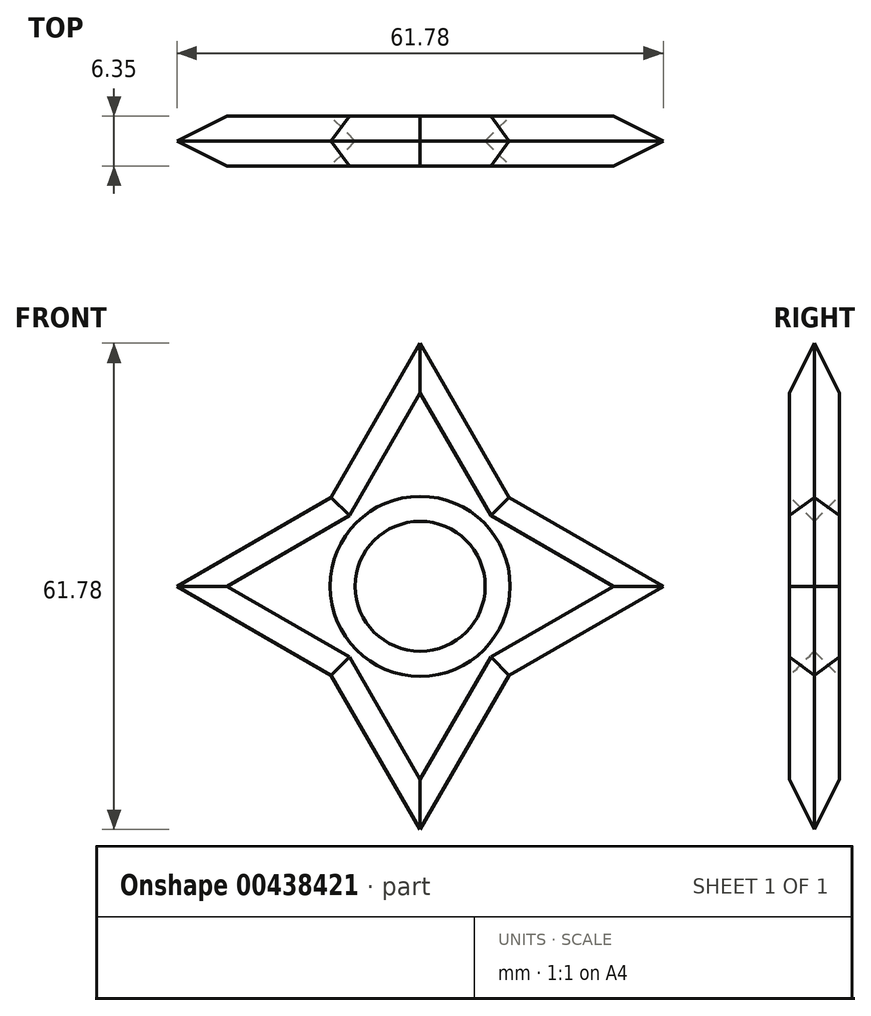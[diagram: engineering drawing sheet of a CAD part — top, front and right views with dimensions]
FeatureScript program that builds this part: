
annotation { "Feature Type Name" : "Feature", "Feature Type Description" : "" }
export const myFeature = defineFeature(function(context is Context, id is Id, definition is map)
    precondition{}
    {
        {
            var Q0;
            Q0=qCreatedBy(makeId("Front.planeOp"),FACE);
            var sketch = newSketch(context, id + "F0", { "sketchPlane" : qUnion([Q0])});
            skLineSegment(sketch, "E0.bottom", {"start": v(0, 0) * mm, "end": v(25.4, 0) * mm});
            skLineSegment(sketch, "E0.top", {"start": v(0, 25.4) * mm, "end": v(25.4, 25.4) * mm});
            skLineSegment(sketch, "E0.left", {"start": v(0, 0) * mm, "end": v(0, 25.4) * mm});
            skLineSegment(sketch, "E0.right", {"start": v(25.4, 0) * mm, "end": v(25.4, 25.4) * mm});
            skLineSegment(sketch, "E1", {"start": v(0, 25.4) * mm, "end": v(12.7, 47.4) * mm});
            skLineSegment(sketch, "E2", {"start": v(12.7, 47.4) * mm, "end": v(25.4, 25.4) * mm});
            skLineSegment(sketch, "E3", {"start": v(0, 25.4) * mm, "end": v(-22, 12.7) * mm});
            skPoint(sketch, "E3.endSnap0", {"position": v(0, 12.7) * mm});
            skLineSegment(sketch, "E4", {"start": v(-22, 12.7) * mm, "end": v(0, 0) * mm});
            skLineSegment(sketch, "E5", {"start": v(0, 0) * mm, "end": v(12.7, -22) * mm});
            skLineSegment(sketch, "E6", {"start": v(12.7, -22) * mm, "end": v(25.4, 0) * mm});
            skLineSegment(sketch, "E7", {"start": v(25.4, 25.4) * mm, "end": v(47.4, 12.7) * mm});
            skLineSegment(sketch, "E8", {"start": v(47.4, 12.7) * mm, "end": v(25.4, 0) * mm});
            skCircle(sketch, "E9", {"center": v(12.7, 12.7) * mm, "radius": 6.35 * mm});
            skSolve(sketch);
        }
        {
            var Q0;
            Q0=makeQuery(id+"F0.imprint","IMPRINT",FACE,{"disambiguationData":[TD([[makeQuery(id+"F0.imprint","IMPRINT",EDGE,{"derivedFrom":sQuery(id+"F0.wireOp",EDGE,"E0.bottom")}),1.0]])]});
            var Q1;
            Q1=makeQuery(id+"F0.imprint","IMPRINT",FACE,{"disambiguationData":[TD([[makeQuery(id+"F0.imprint","IMPRINT",EDGE,{"derivedFrom":sQuery(id+"F0.wireOp",EDGE,"E0.top")}),1.0]])]});
            var Q2;
            Q2=makeQuery(id+"F0.imprint","IMPRINT",FACE,{"disambiguationData":[TD([[makeQuery(id+"F0.imprint","IMPRINT",EDGE,{"derivedFrom":sQuery(id+"F0.wireOp",EDGE,"E0.left")}),1.0]])]});
            var Q3;
            Q3=makeQuery(id+"F0.imprint","IMPRINT",FACE,{"disambiguationData":[TD([[makeQuery(id+"F0.imprint","IMPRINT",EDGE,{"derivedFrom":sQuery(id+"F0.wireOp",EDGE,"E0.right")}),-1.0]])]});
            var Q4;
            Q4=makeQuery(id+"F0.imprint","IMPRINT",FACE,{"disambiguationData":[TD([[makeQuery(id+"F0.imprint","IMPRINT",EDGE,{"derivedFrom":sQuery(id+"F0.wireOp",EDGE,"E0.bottom")}),-1.0]])]});
            extrude(context, id + "F1", {"entities" : qUnion([Q0, Q1, Q2, Q3, Q4]), "depth" : 6.35 * mm});
        }
        {
            var Q0;
            Q0=makeQuery(id+"F1.opExtrude","CAP_FACE",FACE,{"disambiguationData":[OSD([sQuery(id+"F0.wireOp",EDGE,"E1"),sQuery(id+"F0.wireOp",EDGE,"E2"),sQuery(id+"F0.wireOp",EDGE,"E3"),sQuery(id+"F0.wireOp",EDGE,"E4"),sQuery(id+"F0.wireOp",EDGE,"E5"),sQuery(id+"F0.wireOp",EDGE,"E6"),sQuery(id+"F0.wireOp",EDGE,"E7"),sQuery(id+"F0.wireOp",EDGE,"E8")])],"isStart":false});
            chamfer(context, id + "F2", {"entities" : qUnion([Q0]), "width" : 5.08 * mm, "tangentPropagation" : true});
        }
        {
            var Q0;
            Q0=makeQuery(id+"F1.opExtrude","CAP_FACE",FACE,{"disambiguationData":[OSD([sQuery(id+"F0.wireOp",EDGE,"E1"),sQuery(id+"F0.wireOp",EDGE,"E2"),sQuery(id+"F0.wireOp",EDGE,"E3"),sQuery(id+"F0.wireOp",EDGE,"E4"),sQuery(id+"F0.wireOp",EDGE,"E5"),sQuery(id+"F0.wireOp",EDGE,"E6"),sQuery(id+"F0.wireOp",EDGE,"E7"),sQuery(id+"F0.wireOp",EDGE,"E8")])],"isStart":true});
            chamfer(context, id + "F3", {"entities" : qUnion([Q0]), "width" : 5.08 * mm, "tangentPropagation" : true});
        }
    });
